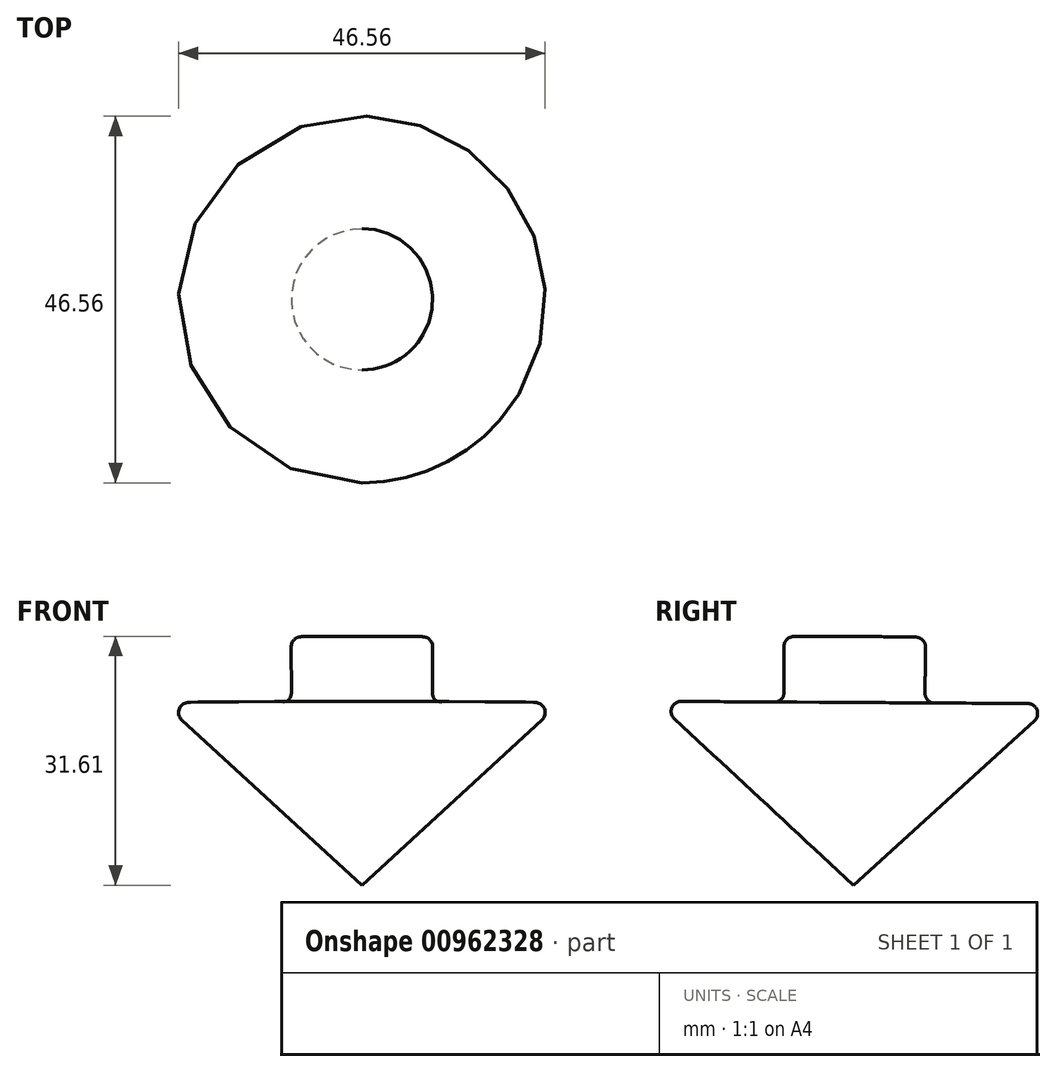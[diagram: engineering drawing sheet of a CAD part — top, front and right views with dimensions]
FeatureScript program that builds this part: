
annotation { "Feature Type Name" : "Feature", "Feature Type Description" : "" }
export const myFeature = defineFeature(function(context is Context, id is Id, definition is map)
    precondition{}
    {
        {
            var Q0;
            Q0=qCreatedBy(makeId("Right.planeOp"),FACE);
            var sketch = newSketch(context, id + "F0", { "sketchPlane" : qUnion([Q0])});
            skLineSegment(sketch, "E0", {"start": v(0, 0) * mm, "end": v(-25.15, 23.37) * mm});
            skLineSegment(sketch, "E1.top", {"start": v(-8.8, 31.6) * mm, "end": v(0.2, 31.6) * mm});
            skLineSegment(sketch, "E1.left", {"start": v(-8.8, 23.22) * mm, "end": v(-8.8, 31.6) * mm});
            skLineSegment(sketch, "E2.trimOffspring", {"start": v(-8.8, 23.22) * mm, "end": v(-25.15, 23.37) * mm});
            skLineSegment(sketch, "E3", {"start": v(0.2, 31.6) * mm, "end": v(0, 0) * mm});
            skSolve(sketch);
        }
        {
            var Q0;
            Q0=makeQuery(id+"F0.imprint","IMPRINT",FACE,{"disambiguationData":[TD([[makeQuery(id+"F0.imprint","IMPRINT",EDGE,{"derivedFrom":sQuery(id+"F0.wireOp",EDGE,"E0")}),-1.0]])]});
            var Q1;
            Q1=sQuery(id+"F0.wireOp",EDGE,"E3");
            revolve(context, id + "F1", {"surfaceOperationType" : NewSurfaceOperationType.NEW, "entities" : qUnion([Q0]), "axis" : qUnion([Q1]), "revolveType" : RevolveType.FULL});
        }
        {
            var Q0;
            Q0=qCreatedBy(makeId("Top.planeOp"),FACE);
            var sketch = newSketch(context, id + "F2", { "sketchPlane" : qUnion([Q0])});
            skCircle(sketch, "E4", {"center": v(0, 0) * mm, "radius": 69.89 * mm});
            skSolve(sketch);
        }
        {
            var Q0;
            Q0=sQuery(id+"F2.wireOp",EDGE,"E4");
            extrude(context, id + "F3", {"bodyType" : ToolBodyType.SURFACE, "surfaceEntities" : qUnion([Q0]), "endBound" : BoundingType.SYMMETRIC, "oppositeDirection" : true, "depth" : 3.8 * mm, "offsetDistance" : 25.4 * mm});
        }
        {
            var Q0;
            Q0=makeQuery(id+"F1.opRevolve","SWEPT_EDGE",EDGE,{"disambiguationData":[OSD([sQuery(id+"F0.wireOp",EDGE,"E0"),sQuery(id+"F0.wireOp",EDGE,"E2.trimOffspring")])]});
            fillet(context, id + "F4", {"entities" : qUnion([Q0]), "radius" : 1.27 * mm, "tangentPropagation" : true, "allowEdgeOverflow" : false});
        }
        {
            var Q0;
            Q0=makeQuery(id+"F1.opRevolve","SWEPT_FACE",FACE,{"disambiguationData":[OSD([sQuery(id+"F0.wireOp",EDGE,"E1.left")])]});
            var Q1;
            Q1=makeQuery(id+"F1.opRevolve","SWEPT_FACE",FACE,{"disambiguationData":[OSD([sQuery(id+"F0.wireOp",EDGE,"E2.trimOffspring")])]});
            var Q2;
            Q2=makeQuery(id+"F1.opRevolve","SWEPT_EDGE",EDGE,{"disambiguationData":[OSD([sQuery(id+"F0.wireOp",EDGE,"E1.left"),sQuery(id+"F0.wireOp",EDGE,"E2.trimOffspring")])]});
            fillet(context, id + "F5", {"entities" : qUnion([Q0, Q1, Q2]), "radius" : 1.27 * mm, "tangentPropagation" : true, "allowEdgeOverflow" : false});
        }
    });
